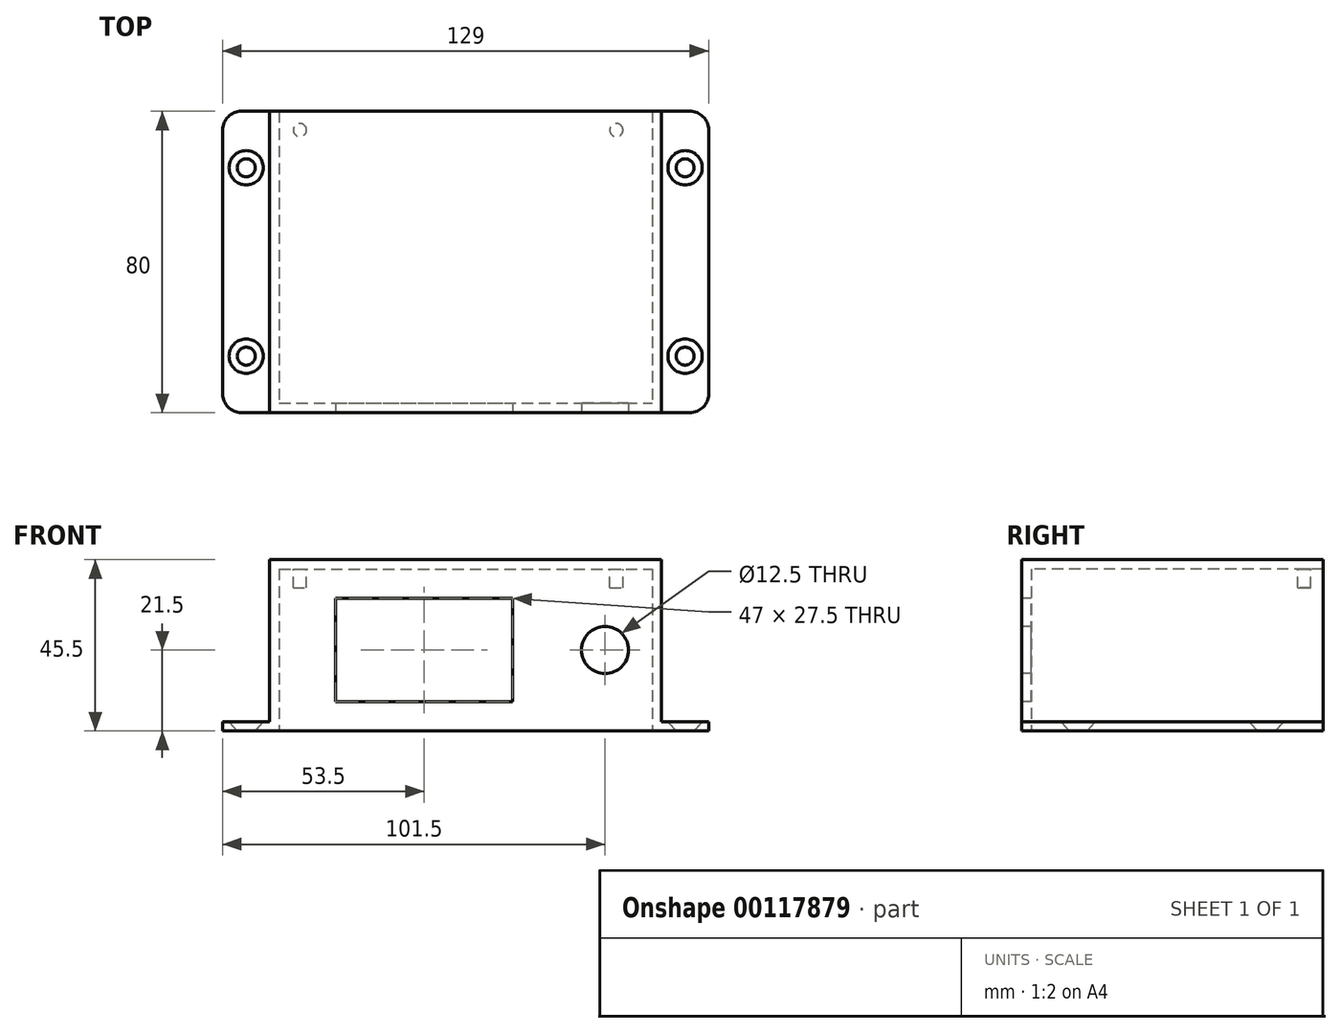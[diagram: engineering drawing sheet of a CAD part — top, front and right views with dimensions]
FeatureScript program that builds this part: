
annotation { "Feature Type Name" : "Feature", "Feature Type Description" : "" }
export const myFeature = defineFeature(function(context is Context, id is Id, definition is map)
    precondition{}
    {
        {
            var Q0;
            Q0=qCreatedBy(makeId("Front.planeOp"),FACE);
            var sketch = newSketch(context, id + "F0", { "sketchPlane" : qUnion([Q0])});
            skLineSegment(sketch, "E0.bottom", {"start": v(0, 0) * mm, "end": v(47, 0) * mm});
            skLineSegment(sketch, "E0.top", {"start": v(0, 27.5) * mm, "end": v(47, 27.5) * mm});
            skLineSegment(sketch, "E0.left", {"start": v(0, 0) * mm, "end": v(0, 27.5) * mm});
            skLineSegment(sketch, "E0.right", {"start": v(47, 0) * mm, "end": v(47, 27.5) * mm});
            skLineSegment(sketch, "E1.bottom", {"start": v(-15, 35.25) * mm, "end": v(84, 35.25) * mm});
            skLineSegment(sketch, "E1.top", {"start": v(-15, -7.75) * mm, "end": v(84, -7.75) * mm});
            skLineSegment(sketch, "E1.left", {"start": v(-15, 35.25) * mm, "end": v(-15, -7.75) * mm});
            skLineSegment(sketch, "E1.right", {"start": v(84, 35.25) * mm, "end": v(84, -7.75) * mm});
            skPoint(sketch, "E2", {"position": v(47, 13.75) * mm});
            skPoint(sketch, "E3", {"position": v(84, 13.75) * mm});
            skLineSegment(sketch, "E4", {"start": v(-15, -7.75) * mm, "end": v(-30, -7.75) * mm});
            skLineSegment(sketch, "E5", {"start": v(-30, -7.75) * mm, "end": v(-30, -5.25) * mm});
            skLineSegment(sketch, "E6", {"start": v(-30, -5.25) * mm, "end": v(-17.5, -5.25) * mm});
            skLineSegment(sketch, "E7", {"start": v(-17.5, -5.25) * mm, "end": v(-17.5, 37.75) * mm});
            skLineSegment(sketch, "E8", {"start": v(-17.5, 37.75) * mm, "end": v(86.5, 37.75) * mm});
            skLineSegment(sketch, "E9", {"start": v(86.5, 37.75) * mm, "end": v(86.5, -5.25) * mm});
            skLineSegment(sketch, "E10", {"start": v(86.5, -5.25) * mm, "end": v(99, -5.25) * mm});
            skLineSegment(sketch, "E11", {"start": v(99, -5.25) * mm, "end": v(99, -7.75) * mm});
            skLineSegment(sketch, "E12", {"start": v(99, -7.75) * mm, "end": v(84, -7.75) * mm});
            skCircle(sketch, "E13", {"center": v(71.5, 13.75) * mm, "radius": 6.25 * mm});
            skSolve(sketch);
        }
        {
            var Q0;
            Q0=makeQuery(id+"F0.imprint","IMPRINT",FACE,{"disambiguationData":[TD([[makeQuery(id+"F0.imprint","IMPRINT",EDGE,{"derivedFrom":sQuery(id+"F0.wireOp",EDGE,"E1.bottom")}),1.0]])]});
            extrude(context, id + "F1", {"entities" : qUnion([Q0]), "oppositeDirection" : true, "depth" : 80 * mm});
        }
        {
            var Q0;
            Q0=makeQuery(id+"F0.imprint","IMPRINT",FACE,{"disambiguationData":[TD([[makeQuery(id+"F0.imprint","IMPRINT",EDGE,{"derivedFrom":sQuery(id+"F0.wireOp",EDGE,"E0.bottom")}),-1.0]])]});
            extrude(context, id + "F2", {"entities" : qUnion([Q0]), "operationType" : NewBodyOperationType.ADD, "oppositeDirection" : true, "depth" : 2.5 * mm});
        }
        {
            var Q0;
            Q0=makeQuery(id+"F1.opExtrude","SWEPT_FACE",FACE,{"disambiguationData":[OSD([sQuery(id+"F0.wireOp",EDGE,"E6")])]});
            var sketch = newSketch(context, id + "F3", { "sketchPlane" : qUnion([Q0])});
            skPoint(sketch, "E14", {"position": v(-23.75, 65) * mm});
            skPoint(sketch, "E15", {"position": v(-23.75, 15) * mm});
            skPoint(sketch, "E16", {"position": v(92.75, 65) * mm});
            skPoint(sketch, "E17", {"position": v(92.75, 15) * mm});
            skPoint(sketch, "E18", {"position": v(-23.75, 80) * mm});
            skSolve(sketch);
        }
        {
            var Q0;
            Q0=sQuery(id+"F3.wireOp",VERTEX,"E14");
            var Q1;
            Q1=sQuery(id+"F3.wireOp",VERTEX,"E15");
            var Q2;
            Q2=sQuery(id+"F3.wireOp",VERTEX,"E17");
            var Q3;
            Q3=sQuery(id+"F3.wireOp",VERTEX,"E16");
            var Q4;
            Q4=makeQuery(id+"F1.opExtrude","SWEPT_BODY",BODY,{"disambiguationData":[OSD([sQuery(id+"F0.wireOp",EDGE,"E1.bottom"),sQuery(id+"F0.wireOp",EDGE,"E1.left"),sQuery(id+"F0.wireOp",EDGE,"E1.right"),sQuery(id+"F0.wireOp",EDGE,"E4"),sQuery(id+"F0.wireOp",EDGE,"E5"),sQuery(id+"F0.wireOp",EDGE,"E6"),sQuery(id+"F0.wireOp",EDGE,"E7"),sQuery(id+"F0.wireOp",EDGE,"E8"),sQuery(id+"F0.wireOp",EDGE,"E9"),sQuery(id+"F0.wireOp",EDGE,"E10"),sQuery(id+"F0.wireOp",EDGE,"E11"),sQuery(id+"F0.wireOp",EDGE,"E12")])]});
            hole(context, id + "F4", {"style" : HoleStyle.C_SINK, "endStyle" : HoleEndStyle.THROUGH, "standardTappedOrClearance" : lookupTablePath({ "standard" : "ANSI", "fit" : "Normal (ASME)", "size" : "#8", "type" : "Clearance" }), "standardBlindInLast" : lookupTablePath({ "fit" : "Free", "standard" : "ANSI", "size" : "#8", "type" : "Clearance" }), "holeDiameter" : 4.5 * mm, "cSinkDiameter" : 9.12 * mm, "cSinkAngle" : 82 * degree, "locations" : qUnion([Q0, Q1, Q2, Q3]), "scope" : qUnion([Q4]), "isTappedThrough" : true});
        }
        {
            var Q0;
            Q0=makeQuery(id+"F1.opExtrude","CAP_EDGE",EDGE,{"disambiguationData":[OSD([sQuery(id+"F0.wireOp",EDGE,"E11")])],"isStart":true});
            var Q1;
            Q1=makeQuery(id+"F1.opExtrude","CAP_EDGE",EDGE,{"disambiguationData":[OSD([sQuery(id+"F0.wireOp",EDGE,"E5")])],"isStart":true});
            var Q2;
            Q2=makeQuery(id+"F1.opExtrude","CAP_EDGE",EDGE,{"disambiguationData":[OSD([sQuery(id+"F0.wireOp",EDGE,"E11")])],"isStart":false});
            var Q3;
            Q3=makeQuery(id+"F1.opExtrude","CAP_EDGE",EDGE,{"disambiguationData":[OSD([sQuery(id+"F0.wireOp",EDGE,"E5")])],"isStart":false});
            fillet(context, id + "F5", {"entities" : qUnion([Q0, Q1, Q2, Q3]), "radius" : 5 * mm, "tangentPropagation" : true, "allowEdgeOverflow" : false});
        }
        {
            var Q0;
            Q0=makeQuery(id+"F1.opExtrude","SWEPT_FACE",FACE,{"disambiguationData":[OSD([sQuery(id+"F0.wireOp",EDGE,"E1.bottom")])]});
            var sketch = newSketch(context, id + "F6", { "sketchPlane" : qUnion([Q0])});
            skLineSegment(sketch, "E19", {"start": v(-9.5, 6.46) * mm, "end": v(-9.5, -86.26) * mm, "construction": true});
            skLineSegment(sketch, "E20", {"start": v(74.5, 5.28) * mm, "end": v(74.5, -90.64) * mm, "construction": true});
            skPoint(sketch, "E21", {"position": v(-9.5, -75) * mm});
            skPoint(sketch, "E22", {"position": v(74.5, -75) * mm});
            skCircle(sketch, "E23", {"center": v(-9.5, -75) * mm, "radius": 1.75 * mm});
            skCircle(sketch, "E24", {"center": v(74.5, -75) * mm, "radius": 1.75 * mm});
            skSolve(sketch);
        }
        {
            var Q0;
            Q0=makeQuery(id+"F6.imprint","IMPRINT",FACE,{"disambiguationData":[TD([[makeQuery(id+"F6.imprint","IMPRINT",EDGE,{"derivedFrom":sQuery(id+"F6.wireOp",EDGE,"E23")}),1.0]])]});
            var Q1;
            Q1=makeQuery(id+"F6.imprint","IMPRINT",FACE,{"disambiguationData":[TD([[makeQuery(id+"F6.imprint","IMPRINT",EDGE,{"derivedFrom":sQuery(id+"F6.wireOp",EDGE,"E24")}),1.0]])]});
            extrude(context, id + "F7", {"entities" : qUnion([Q0, Q1]), "operationType" : NewBodyOperationType.ADD, "depth" : 5 * mm});
        }
    });
